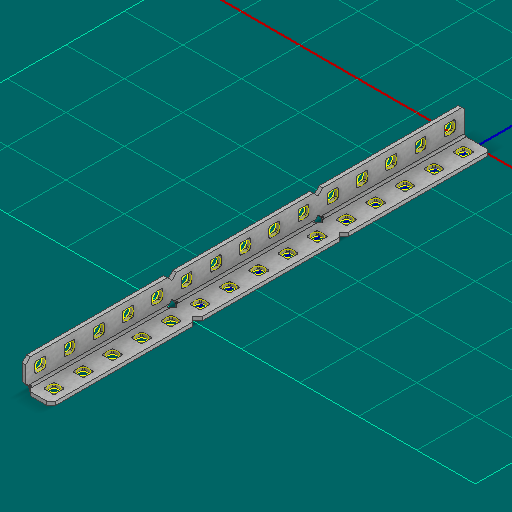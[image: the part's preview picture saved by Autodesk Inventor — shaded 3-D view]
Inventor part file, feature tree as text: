
AUTODESK INVENTOR PART (.ipt)
format: ipt  version: 2025 (Build 290162000, 162)  size: 726,528 bytes
history: native  units: in
note: dims shown in document units (in); Inventor stores cm internally (conversion verified against a paired STEP export)
features: other x69, sketch x2, sheet_metal_op x1
ambient origin geometry x8: Origin, YZ Plane, XZ Plane, XY Plane, X Axis, Y Axis, Z Axis, Center Point
bodies: Solid1 (feature_tree)
feature tree (72):
  other  "Alu Angle 1x1x15.ipt"
  other  "Solid1::Alu Angle 1x1x15.ipt"
  other  "TaggingFeature1"
  sketch  "Sketch1"  dims[d0=0.3937in]
  sketch  "Sketch2"  dims[d1=0.0625in]
  sheet_metal_op  "Body Pattern Sketch"
  other  "Arc Length"
  other  "Diagonal Plane"
  other  "Srf1"
  other  "Srf2"
  other  "Srf3"
  other  "Srf4"
  other  "Srf5"
  other  "Srf6"
  other  "Srf7"
  other  "Srf8"
  other  "Srf9"
  other  "Srf10"
  other  "Srf11"
  other  "Srf12"
  other  "Srf13"
  other  "Srf14"
  other  "Srf15"
  other  "Srf16"
  other  "Srf17"
  other  "Srf18"
  other  "Srf19"
  other  "Srf20"
  other  "Srf21"
  other  "Srf22"
  other  "Srf23"
  other  "Srf24"
  other  "Srf25"
  other  "Srf26"
  other  "Srf27"
  other  "Srf28"
  other  "Srf29"
  other  "Srf30"
  other  "Srf31"
  other  "Srf32"
  other  "Srf91::Derived"
  other  "Srf92::Derived"
  other  "Srf856::Derived"
  other  "Srf857::Derived"
  other  "Srf858::Derived"
  other  "Srf859::Derived"
  other  "Srf860::Derived"
  other  "Srf861::Derived"
  other  "Srf1383::Derived"
  other  "Srf1384::Derived"
  other  "Srf1385::Derived"
  other  "Srf1386::Derived"
  other  "Srf1387::Derived"
  other  "Srf1388::Derived"
  other  "Srf1389::Derived"
  other  "Srf1390::Derived"
  other  "Srf1275::Derived"
  other  "Srf1276::Derived"
  other  "Srf1278::Derived"
  other  "Srf1279::Derived"
  other  "Srf1280::Derived"
  other  "Srf1281::Derived"
  other  "Srf1282::Derived"
  other  "Srf1283::Derived"
  other  "Srf1475::Derived"
  other  "Srf1476::Derived"
  other  "Srf1477::Derived"
  other  "Srf1478::Derived"
  other  "Srf1479::Derived"
  other  "Srf1480::Derived"
  other  "Srf1481::Derived"
  other  "Srf1482::Derived"
